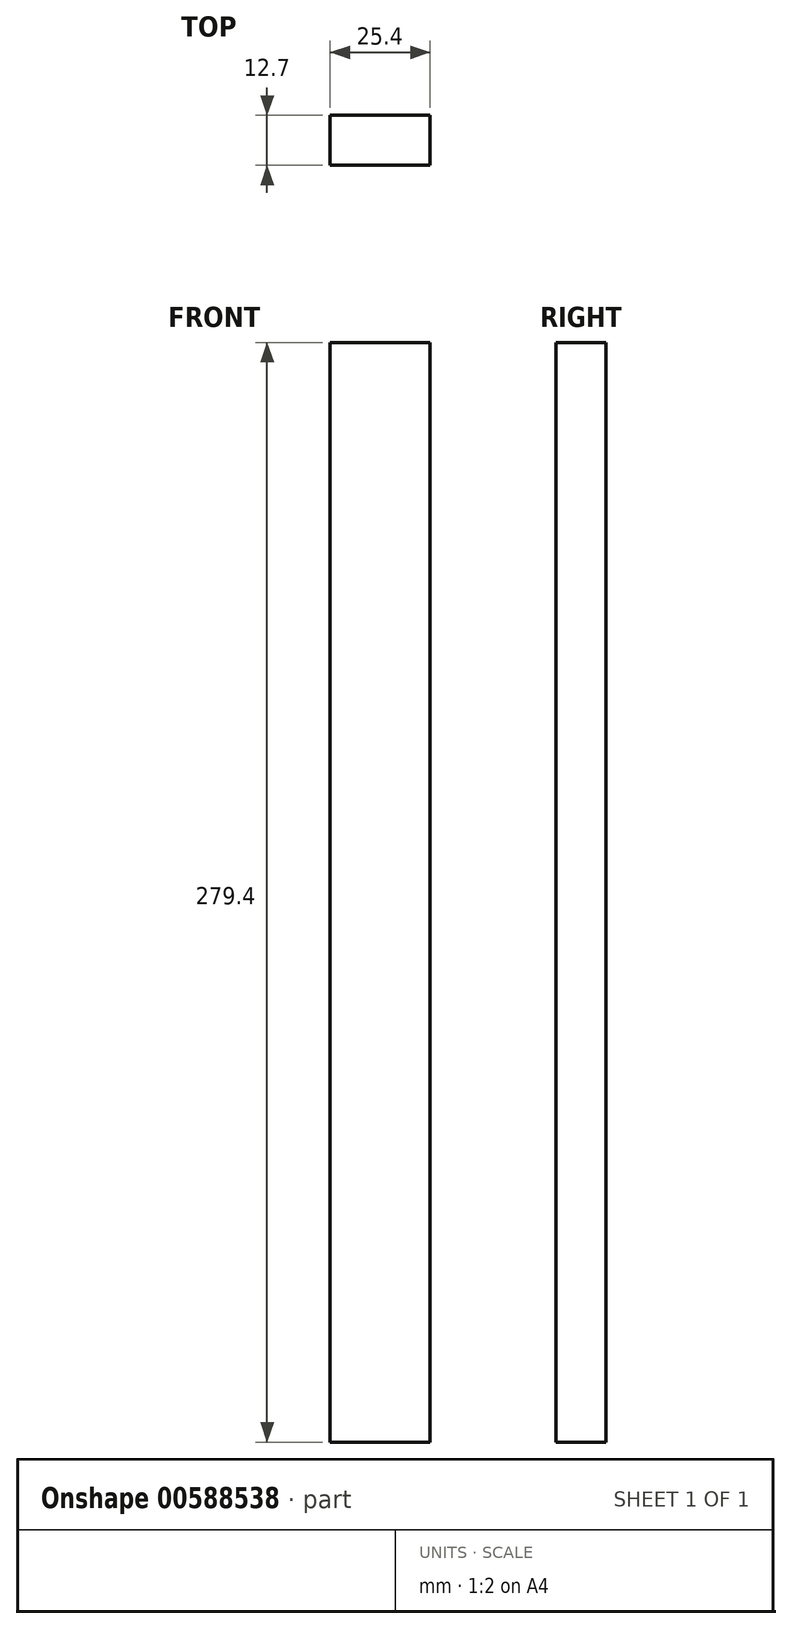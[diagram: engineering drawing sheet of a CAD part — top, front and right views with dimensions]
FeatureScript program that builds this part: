
annotation { "Feature Type Name" : "Feature", "Feature Type Description" : "" }
export const myFeature = defineFeature(function(context is Context, id is Id, definition is map)
    precondition{}
    {
        {
            var Q0;
            Q0=qCreatedBy(makeId("Right.planeOp"),FACE);
            var sketch = newSketch(context, id + "F0", { "sketchPlane" : qUnion([Q0])});
            skLineSegment(sketch, "E0", {"start": v(0, 0) * mm, "end": v(52.38, 0) * mm});
            skLineSegment(sketch, "E1.bottom", {"start": v(0, 139.7) * mm, "end": v(12.7, 139.7) * mm});
            skLineSegment(sketch, "E1.top", {"start": v(0, 0) * mm, "end": v(12.7, 0) * mm});
            skLineSegment(sketch, "E1.left", {"start": v(0, 139.7) * mm, "end": v(0, 0) * mm});
            skLineSegment(sketch, "E1.right", {"start": v(12.7, 139.7) * mm, "end": v(12.7, 0) * mm});
            skLineSegment(sketch, "E2.MirrorCS", {"start": v(12.7, -139.7) * mm, "end": v(12.7, 0) * mm});
            skLineSegment(sketch, "E3.MirrorCS", {"start": v(0, -139.7) * mm, "end": v(12.7, -139.7) * mm});
            skLineSegment(sketch, "E4.MirrorCS", {"start": v(0, -139.7) * mm, "end": v(0, 0) * mm});
            skSolve(sketch);
        }
        {
            var Q0;
            Q0 = qSketchRegion(id + "F0", true);
            extrude(context, id + "F1", {"entities" : qUnion([Q0]), "depth" : 25.4 * mm, "offsetDistance" : 25.4 * mm});
        }
    });
